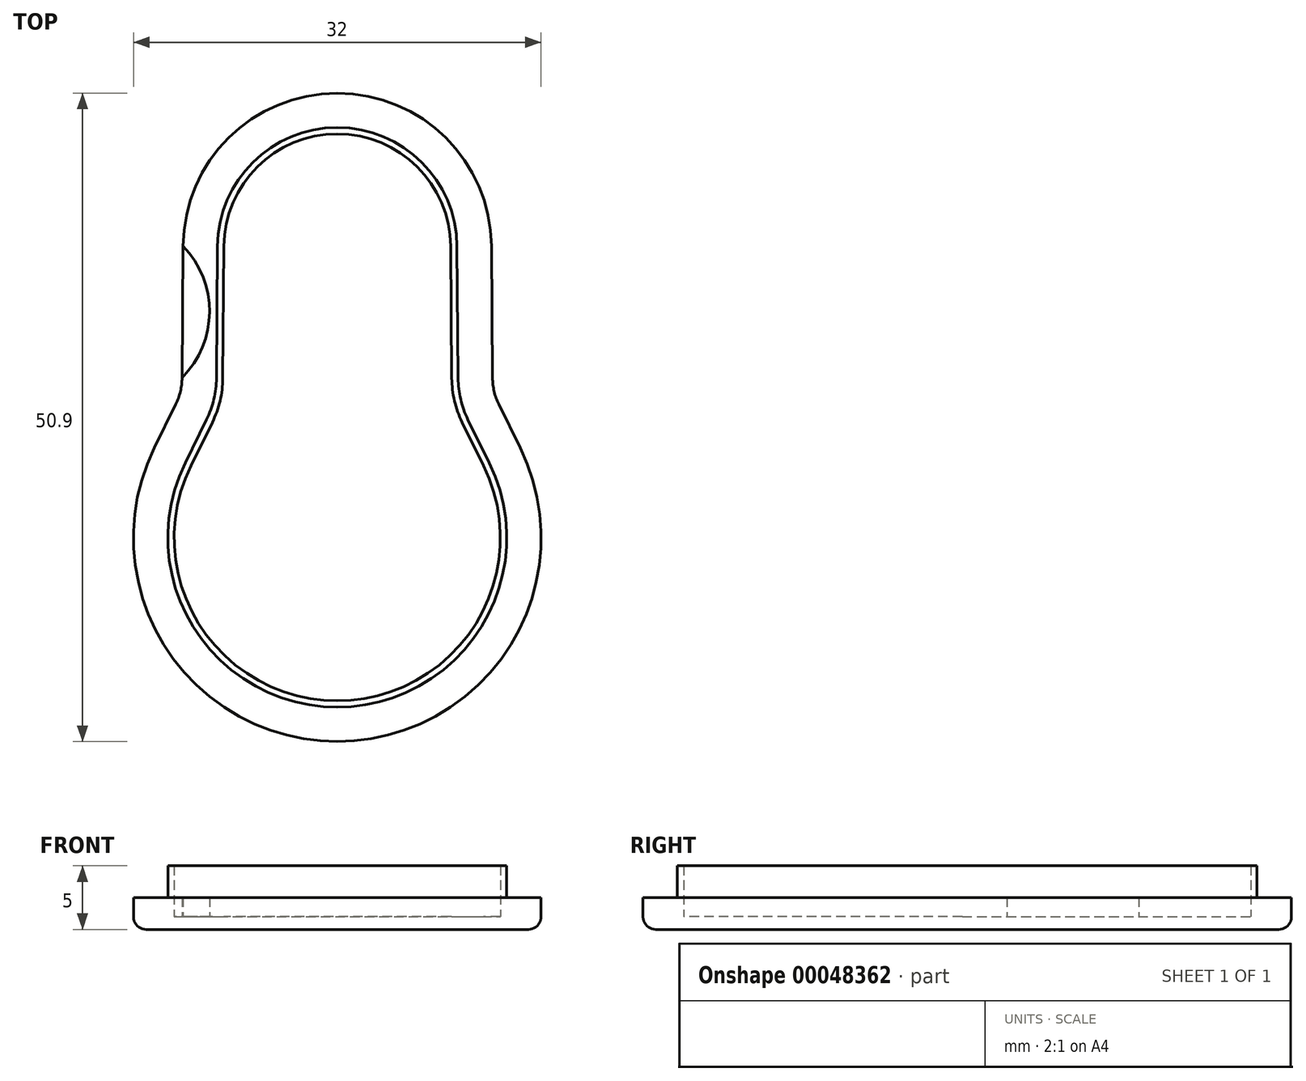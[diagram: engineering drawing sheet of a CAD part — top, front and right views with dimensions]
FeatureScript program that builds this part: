
annotation { "Feature Type Name" : "Feature", "Feature Type Description" : "" }
export const myFeature = defineFeature(function(context is Context, id is Id, definition is map)
    precondition{}
    {
        {
            var Q0;
            Q0=qCreatedBy(makeId("Top.planeOp"),FACE);
            var sketch = newSketch(context, id + "F0", { "sketchPlane" : qUnion([Q0])});
            skArc(sketch, "E0", {"start": v(-11.48, 5.65) * mm, "mid": v(0, -12.8) * mm, "end": v(11.48, 5.65) * mm});
            skLineSegment(sketch, "E1", {"start": v(0, -12.8) * mm, "end": v(0, 31.7) * mm, "construction": true});
            skArc(sketch, "E2", {"start": v(8.9, 22.87) * mm, "mid": v(0, 31.7) * mm, "end": v(-8.9, 22.87) * mm});
            skLineSegment(sketch, "E3", {"start": v(0, 31.7) * mm, "end": v(0, 22.8) * mm, "construction": true});
            skLineSegment(sketch, "E4", {"start": v(0, 31.7) * mm, "end": v(0, 10.7) * mm, "construction": true});
            skLineSegment(sketch, "E5", {"start": v(0, 10.7) * mm, "end": v(9, 10.7) * mm, "construction": true});
            skLineSegment(sketch, "E6.MirrorCS", {"start": v(0, 10.7) * mm, "end": v(-9, 10.7) * mm, "construction": true});
            skLineSegment(sketch, "E7", {"start": v(-8.98, 12.53) * mm, "end": v(-8.9, 22.87) * mm});
            skLineSegment(sketch, "E8", {"start": v(8.98, 12.53) * mm, "end": v(8.9, 22.87) * mm});
            skLineSegment(sketch, "E9", {"start": v(-9.8, 9.06) * mm, "end": v(-11.48, 5.65) * mm});
            skLineSegment(sketch, "E10", {"start": v(9.8, 9.06) * mm, "end": v(11.48, 5.65) * mm});
            skPoint(sketch, "E11.visualSharp", {"position": v(-9, 10.7) * mm});
            skArc(sketch, "E11.filletArc", {"start": v(-9.8, 9.06) * mm, "mid": v(-9.2, 10.75) * mm, "end": v(-8.98, 12.53) * mm});
            skPoint(sketch, "E12.visualSharp", {"position": v(9, 10.7) * mm});
            skArc(sketch, "E12.filletArc", {"start": v(8.98, 12.53) * mm, "mid": v(9.2, 10.75) * mm, "end": v(9.8, 9.06) * mm});
            skSolve(sketch);
        }
        {
            var Q0;
            Q0=makeQuery(id+"F0.imprint","IMPRINT",FACE,{"disambiguationData":[TD([[makeQuery(id+"F0.imprint","IMPRINT",EDGE,{"derivedFrom":sQuery(id+"F0.wireOp",EDGE,"E0")}),1.0]])]});
            var sketch = newSketch(context, id + "F1", { "sketchPlane" : qUnion([Q0])});
            skLineSegment(sketch, "E13.0", {"start": v(-8.98, 12.53) * mm, "end": v(-8.9, 22.87) * mm});
            skArc(sketch, "E14.0", {"start": v(8.9, 22.87) * mm, "mid": v(0, 31.7) * mm, "end": v(-8.9, 22.87) * mm});
            skLineSegment(sketch, "E15.0", {"start": v(8.98, 12.53) * mm, "end": v(8.9, 22.87) * mm});
            skArc(sketch, "E16.0", {"start": v(8.98, 12.53) * mm, "mid": v(9.2, 10.75) * mm, "end": v(9.8, 9.06) * mm});
            skLineSegment(sketch, "E17.0", {"start": v(9.8, 9.06) * mm, "end": v(11.48, 5.65) * mm});
            skArc(sketch, "E18.0", {"start": v(-11.48, 5.65) * mm, "mid": v(0, -12.8) * mm, "end": v(11.48, 5.65) * mm});
            skLineSegment(sketch, "E19.0", {"start": v(-9.8, 9.06) * mm, "end": v(-11.48, 5.65) * mm});
            skArc(sketch, "E20.0", {"start": v(-9.8, 9.06) * mm, "mid": v(-9.2, 10.75) * mm, "end": v(-8.98, 12.53) * mm});
            skArc(sketch, "E21.0", {"start": v(-10.26, 9.28) * mm, "mid": v(-9.69, 10.86) * mm, "end": v(-9.48, 12.53) * mm});
            skLineSegment(sketch, "E21.1", {"start": v(-10.26, 9.28) * mm, "end": v(-11.93, 5.87) * mm});
            skLineSegment(sketch, "E21.2", {"start": v(-9.48, 12.53) * mm, "end": v(-9.4, 22.88) * mm});
            skArc(sketch, "E21.3", {"start": v(-11.93, 5.87) * mm, "mid": v(0, -13.3) * mm, "end": v(11.93, 5.87) * mm});
            skArc(sketch, "E21.4", {"start": v(9.4, 22.88) * mm, "mid": v(0, 32.2) * mm, "end": v(-9.4, 22.88) * mm});
            skLineSegment(sketch, "E21.5", {"start": v(9.48, 12.53) * mm, "end": v(9.4, 22.88) * mm});
            skArc(sketch, "E21.6", {"start": v(9.48, 12.53) * mm, "mid": v(9.69, 10.86) * mm, "end": v(10.26, 9.28) * mm});
            skLineSegment(sketch, "E21.7", {"start": v(10.26, 9.28) * mm, "end": v(11.93, 5.87) * mm});
            skSolve(sketch);
        }
        {
            var Q0;
            Q0=makeQuery(id+"F1.imprint","IMPRINT",FACE,{"disambiguationData":[TD([[makeQuery(id+"F1.imprint","IMPRINT",EDGE,{"derivedFrom":sQuery(id+"F1.wireOp",EDGE,"E13.0")}),1.0]])]});
            extrude(context, id + "F2", {"entities" : qUnion([Q0]), "depth" : 4 * mm});
        }
        {
            var Q0;
            Q0=makeQuery(id+"F0.imprint","IMPRINT",FACE,{"disambiguationData":[TD([[makeQuery(id+"F0.imprint","IMPRINT",EDGE,{"derivedFrom":sQuery(id+"F0.wireOp",EDGE,"E0")}),1.0]])]});
            var sketch = newSketch(context, id + "F3", { "sketchPlane" : qUnion([Q0])});
            skArc(sketch, "E22.0", {"start": v(8.9, 22.87) * mm, "mid": v(0, 31.7) * mm, "end": v(-8.9, 22.87) * mm});
            skLineSegment(sketch, "E23.0", {"start": v(-8.98, 12.53) * mm, "end": v(-8.9, 22.87) * mm});
            skArc(sketch, "E24.0", {"start": v(-9.8, 9.06) * mm, "mid": v(-9.2, 10.75) * mm, "end": v(-8.98, 12.53) * mm});
            skLineSegment(sketch, "E25.0", {"start": v(-9.8, 9.06) * mm, "end": v(-11.48, 5.65) * mm});
            skArc(sketch, "E26.0", {"start": v(-11.48, 5.65) * mm, "mid": v(0, -12.8) * mm, "end": v(11.48, 5.65) * mm});
            skLineSegment(sketch, "E27.0", {"start": v(9.8, 9.06) * mm, "end": v(11.48, 5.65) * mm});
            skArc(sketch, "E28.0", {"start": v(8.98, 12.53) * mm, "mid": v(9.2, 10.75) * mm, "end": v(9.8, 9.06) * mm});
            skLineSegment(sketch, "E29.0", {"start": v(8.98, 12.53) * mm, "end": v(8.9, 22.87) * mm});
            skLineSegment(sketch, "E30.0", {"start": v(12.18, 12.55) * mm, "end": v(12.1, 22.9) * mm});
            skArc(sketch, "E30.1", {"start": v(12.18, 12.55) * mm, "mid": v(12.31, 11.49) * mm, "end": v(12.68, 10.47) * mm});
            skArc(sketch, "E30.2", {"start": v(12.1, 22.9) * mm, "mid": v(0, 34.9) * mm, "end": v(-12.1, 22.9) * mm});
            skLineSegment(sketch, "E30.3", {"start": v(12.68, 10.47) * mm, "end": v(14.36, 7.07) * mm});
            skLineSegment(sketch, "E30.4", {"start": v(-12.18, 12.55) * mm, "end": v(-12.1, 22.9) * mm});
            skArc(sketch, "E30.5", {"start": v(-12.68, 10.47) * mm, "mid": v(-12.31, 11.49) * mm, "end": v(-12.18, 12.55) * mm});
            skLineSegment(sketch, "E30.6", {"start": v(-12.68, 10.47) * mm, "end": v(-14.36, 7.07) * mm});
            skArc(sketch, "E30.7", {"start": v(-14.36, 7.07) * mm, "mid": v(0, -16) * mm, "end": v(14.36, 7.07) * mm});
            skSolve(sketch);
        }
        {
            var Q0;
            Q0=makeQuery(id+"F3.imprint","IMPRINT",FACE,{"disambiguationData":[TD([[makeQuery(id+"F3.imprint","IMPRINT",EDGE,{"derivedFrom":sQuery(id+"F3.wireOp",EDGE,"E22.0")}),-1.0]])]});
            var Q1;
            Q1=makeQuery(id+"F0.imprint","IMPRINT",FACE,{"disambiguationData":[TD([[makeQuery(id+"F0.imprint","IMPRINT",EDGE,{"derivedFrom":sQuery(id+"F0.wireOp",EDGE,"E0")}),1.0]])]});
            extrude(context, id + "F4", {"entities" : qUnion([Q0, Q1]), "operationType" : NewBodyOperationType.ADD, "oppositeDirection" : true, "depth" : 1 * mm});
        }
        {
            var Q0;
            Q0=makeQuery(id+"F4.opExtrude","CAP_EDGE",EDGE,{"disambiguationData":[OSD([sQuery(id+"F3.wireOp",EDGE,"E30.7")])],"isStart":false});
            var Q1;
            Q1=makeQuery(id+"F4.opExtrude","CAP_EDGE",EDGE,{"disambiguationData":[OSD([sQuery(id+"F3.wireOp",EDGE,"E30.6")])],"isStart":false});
            var Q2;
            Q2=makeQuery(id+"F4.opExtrude","CAP_EDGE",EDGE,{"disambiguationData":[OSD([sQuery(id+"F3.wireOp",EDGE,"E30.5")])],"isStart":false});
            var Q3;
            Q3=makeQuery(id+"F4.opExtrude","CAP_EDGE",EDGE,{"disambiguationData":[OSD([sQuery(id+"F3.wireOp",EDGE,"E30.4")])],"isStart":false});
            var Q4;
            Q4=makeQuery(id+"F4.opExtrude","CAP_EDGE",EDGE,{"disambiguationData":[OSD([sQuery(id+"F3.wireOp",EDGE,"E30.2")])],"isStart":false});
            var Q5;
            Q5=makeQuery(id+"F4.opExtrude","CAP_EDGE",EDGE,{"disambiguationData":[OSD([sQuery(id+"F3.wireOp",EDGE,"E30.0")])],"isStart":false});
            var Q6;
            Q6=makeQuery(id+"F4.opExtrude","CAP_EDGE",EDGE,{"disambiguationData":[OSD([sQuery(id+"F3.wireOp",EDGE,"E30.1")])],"isStart":false});
            var Q7;
            Q7=makeQuery(id+"F4.opExtrude","CAP_EDGE",EDGE,{"disambiguationData":[OSD([sQuery(id+"F3.wireOp",EDGE,"E30.3")])],"isStart":false});
            fillet(context, id + "F5", {"entities" : qUnion([Q0, Q1, Q2, Q3, Q4, Q5, Q6, Q7]), "radius" : 1 * mm, "tangentPropagation" : true, "allowEdgeOverflow" : false});
        }
        {
            var Q0;
            Q0=makeQuery(id+"F4.boolean.opBoolean","MERGE",FACE,{"disambiguationData":[OD(0.0)],"derivedFrom":[makeQuery(id+"F4.opExtrude","CAP_FACE",FACE,{"disambiguationData":[OSD([sQuery(id+"F0.wireOp",EDGE,"E0"),sQuery(id+"F0.wireOp",EDGE,"E2"),sQuery(id+"F0.wireOp",EDGE,"E7"),sQuery(id+"F0.wireOp",EDGE,"E8"),sQuery(id+"F0.wireOp",EDGE,"E9"),sQuery(id+"F0.wireOp",EDGE,"E10"),sQuery(id+"F0.wireOp",EDGE,"E11.filletArc"),sQuery(id+"F0.wireOp",EDGE,"E12.filletArc")])],"isStart":true}),makeQuery(id+"F4.opExtrude","CAP_FACE",FACE,{"disambiguationData":[OSD([sQuery(id+"F3.wireOp",EDGE,"E22.0"),sQuery(id+"F3.wireOp",EDGE,"E23.0"),sQuery(id+"F3.wireOp",EDGE,"E24.0"),sQuery(id+"F3.wireOp",EDGE,"E25.0"),sQuery(id+"F3.wireOp",EDGE,"E26.0"),sQuery(id+"F3.wireOp",EDGE,"E27.0"),sQuery(id+"F3.wireOp",EDGE,"E28.0"),sQuery(id+"F3.wireOp",EDGE,"E29.0"),sQuery(id+"F3.wireOp",EDGE,"E30.0"),sQuery(id+"F3.wireOp",EDGE,"E30.1"),sQuery(id+"F3.wireOp",EDGE,"E30.2"),sQuery(id+"F3.wireOp",EDGE,"E30.3"),sQuery(id+"F3.wireOp",EDGE,"E30.4"),sQuery(id+"F3.wireOp",EDGE,"E30.5"),sQuery(id+"F3.wireOp",EDGE,"E30.6"),sQuery(id+"F3.wireOp",EDGE,"E30.7")])],"isStart":true})]});
            var sketch = newSketch(context, id + "F6", { "sketchPlane" : qUnion([Q0])});
            skArc(sketch, "E31.0", {"start": v(-12.68, 10.47) * mm, "mid": v(-12.31, 11.49) * mm, "end": v(-12.18, 12.55) * mm});
            skLineSegment(sketch, "E32.0", {"start": v(-12.68, 10.47) * mm, "end": v(-14.36, 7.07) * mm});
            skArc(sketch, "E33.0", {"start": v(-14.36, 7.07) * mm, "mid": v(0, -16) * mm, "end": v(14.36, 7.07) * mm});
            skLineSegment(sketch, "E34.0", {"start": v(12.68, 10.47) * mm, "end": v(14.36, 7.07) * mm});
            skArc(sketch, "E35.0", {"start": v(12.18, 12.55) * mm, "mid": v(12.31, 11.49) * mm, "end": v(12.68, 10.47) * mm});
            skLineSegment(sketch, "E36.0", {"start": v(12.18, 12.55) * mm, "end": v(12.1, 22.9) * mm});
            skArc(sketch, "E37.0", {"start": v(12.1, 22.9) * mm, "mid": v(0, 34.9) * mm, "end": v(-12.1, 22.9) * mm});
            skLineSegment(sketch, "E38.0", {"start": v(-9.48, 12.53) * mm, "end": v(-9.4, 22.88) * mm});
            skArc(sketch, "E39.0", {"start": v(-10.26, 9.28) * mm, "mid": v(-9.69, 10.86) * mm, "end": v(-9.48, 12.53) * mm});
            skLineSegment(sketch, "E40.0", {"start": v(-10.26, 9.28) * mm, "end": v(-11.93, 5.87) * mm});
            skArc(sketch, "E41.0", {"start": v(-11.93, 5.87) * mm, "mid": v(0, -13.3) * mm, "end": v(11.93, 5.87) * mm});
            skLineSegment(sketch, "E42.0", {"start": v(10.26, 9.28) * mm, "end": v(11.93, 5.87) * mm});
            skArc(sketch, "E43.0", {"start": v(9.48, 12.53) * mm, "mid": v(9.69, 10.86) * mm, "end": v(10.26, 9.28) * mm});
            skLineSegment(sketch, "E44.0", {"start": v(9.48, 12.53) * mm, "end": v(9.4, 22.88) * mm});
            skArc(sketch, "E45.0", {"start": v(9.4, 22.88) * mm, "mid": v(0, 32.2) * mm, "end": v(-9.4, 22.88) * mm});
            skArc(sketch, "E46", {"start": v(-12.18, 12.55) * mm, "mid": v(-10.03, 17.7) * mm, "end": v(-12.1, 22.9) * mm});
            skSolve(sketch);
        }
        {
            var Q0;
            Q0=makeQuery(id+"F6.imprint","IMPRINT",FACE,{"disambiguationData":[TD([[makeQuery(id+"F6.imprint","IMPRINT",EDGE,{"derivedFrom":sQuery(id+"F6.wireOp",EDGE,"E31.0")}),-1.0]])]});
            extrude(context, id + "F7", {"entities" : qUnion([Q0]), "operationType" : NewBodyOperationType.ADD, "depth" : 1.5 * mm});
        }
    });
